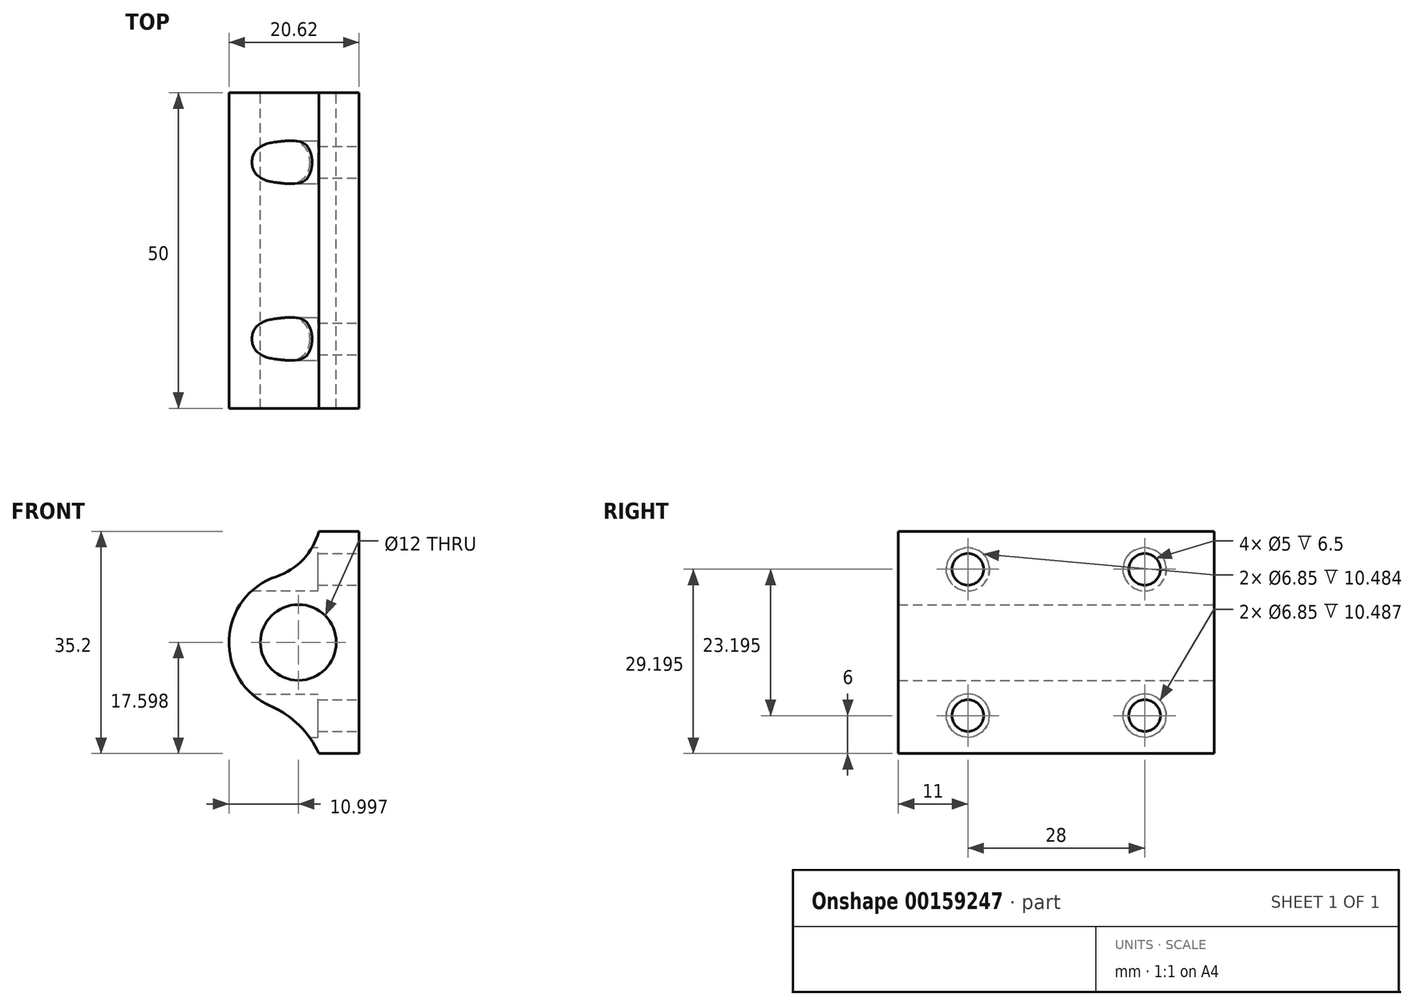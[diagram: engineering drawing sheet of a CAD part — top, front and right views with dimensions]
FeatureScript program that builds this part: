
annotation { "Feature Type Name" : "Feature", "Feature Type Description" : "" }
export const myFeature = defineFeature(function(context is Context, id is Id, definition is map)
    precondition{}
    {
        {
            var Q0;
            Q0=qCreatedBy(makeId("Front.planeOp"),FACE);
            var sketch = newSketch(context, id + "F0", { "sketchPlane" : qUnion([Q0])});
            skLineSegment(sketch, "E0", {"start": v(0, 35.2) * mm, "end": v(0, 0) * mm});
            skLineSegment(sketch, "E1", {"start": v(0, 0) * mm, "end": v(-6.38, 0) * mm});
            skLineSegment(sketch, "E2", {"start": v(0, 17.6) * mm, "end": v(-19.25, 17.6) * mm, "construction": true});
            skCircle(sketch, "E3", {"center": v(-9.62, 17.6) * mm, "radius": 6 * mm});
            skLineSegment(sketch, "E4", {"start": v(0, 35.2) * mm, "end": v(-6.38, 35.2) * mm});
            skPoint(sketch, "E5.orphan", {"position": v(-12.38, 22.93) * mm});
            skPoint(sketch, "E6.orphan", {"position": v(-12.38, 12.27) * mm});
            skArc(sketch, "E7.0", {"start": v(-13.1, 28.03) * mm, "mid": v(-20.61, 18.06) * mm, "end": v(-13.98, 7.5) * mm});
            skArc(sketch, "E8", {"start": v(-13.1, 28.03) * mm, "mid": v(-8.84, 30.76) * mm, "end": v(-6.38, 35.2) * mm});
            skArc(sketch, "E9", {"start": v(-6.38, 0) * mm, "mid": v(-9.47, 4.46) * mm, "end": v(-13.98, 7.5) * mm});
            skSolve(sketch);
        }
        {
            var Q0;
            Q0 = qSketchRegion(id + "F0", true);
            extrude(context, id + "F1", {"entities" : qUnion([Q0]), "depth" : 50 * mm});
        }
        {
            var Q0;
            Q0=makeQuery(id+"F1.opExtrude","SWEPT_FACE",FACE,{"disambiguationData":[OSD([sQuery(id+"F0.wireOp",EDGE,"E0")])]});
            var sketch = newSketch(context, id + "F2", { "sketchPlane" : qUnion([Q0])});
            skLineSegment(sketch, "E10.0", {"start": v(-50, 35.2) * mm, "end": v(0, 35.2) * mm, "construction": true});
            skLineSegment(sketch, "E11", {"start": v(-50, 23.6) * mm, "end": v(0, 23.6) * mm, "construction": true});
            skLineSegment(sketch, "E12", {"start": v(-50, 11.6) * mm, "end": v(0, 11.6) * mm, "construction": true});
            skLineSegment(sketch, "E13", {"start": v(-39, 35.2) * mm, "end": v(-39, 0) * mm, "construction": true});
            skLineSegment(sketch, "E14", {"start": v(-11, 35.2) * mm, "end": v(-11, 0) * mm, "construction": true});
            skCircle(sketch, "E15", {"center": v(-39, 29.2) * mm, "radius": 2.5 * mm});
            skCircle(sketch, "E16", {"center": v(-11, 29.2) * mm, "radius": 2.5 * mm});
            skLineSegment(sketch, "E17", {"start": v(-50, 17.6) * mm, "end": v(0, 17.6) * mm, "construction": true});
            skCircle(sketch, "E18.MirrorC", {"center": v(-39, 6) * mm, "radius": 2.5 * mm});
            skCircle(sketch, "E19.MirrorC", {"center": v(-11, 6) * mm, "radius": 2.5 * mm});
            skPoint(sketch, "E20.0.start.orphan", {"position": v(-50, 0) * mm});
            skPoint(sketch, "E21.0.end.orphan", {"position": v(0, 0) * mm});
            skSolve(sketch);
        }
        {
            var Q0;
            Q0 = qSketchRegion(id + "F2", true);
            extrude(context, id + "F3", {"entities" : qUnion([Q0]), "operationType" : NewBodyOperationType.REMOVE, "oppositeDirection" : true, "depth" : 25 * mm});
        }
        {
            var Q0;
            Q0=qCreatedBy(makeId("Right.planeOp"),FACE);
            cPlane(context, id + "F4", {"entities" : qUnion([Q0]), "cplaneType" : CPlaneType.OFFSET, "offset" : 6.5 * mm, "oppositeDirection" : true, "width" : 150 * mm, "height" : 150 * mm});
        }
        {
            var Q0;
            Q0=qCreatedBy(id+"F4.planeOp",FACE);
            var sketch = newSketch(context, id + "F5", { "sketchPlane" : qUnion([Q0])});
            skArc(sketch, "E22.0", {"start": v(-13, 7.5) * mm, "mid": v(-11, 3.5) * mm, "end": v(-9, 7.5) * mm});
            skArc(sketch, "E23.0", {"start": v(-8.79, 28.03) * mm, "mid": v(-11, 31.7) * mm, "end": v(-13.21, 28.03) * mm});
            skArc(sketch, "E24.0", {"start": v(-41, 7.5) * mm, "mid": v(-39, 3.5) * mm, "end": v(-37, 7.5) * mm});
            skArc(sketch, "E25.0", {"start": v(-36.79, 28.03) * mm, "mid": v(-39, 31.7) * mm, "end": v(-41.21, 28.03) * mm});
            skCircle(sketch, "E26", {"center": v(-11, 6) * mm, "radius": 3.42 * mm});
            skCircle(sketch, "E27", {"center": v(-39, 6) * mm, "radius": 3.42 * mm});
            skCircle(sketch, "E28", {"center": v(-11, 29.2) * mm, "radius": 3.42 * mm});
            skCircle(sketch, "E29", {"center": v(-39, 29.2) * mm, "radius": 3.42 * mm});
            skSolve(sketch);
        }
        {
            var Q0;
            Q0 = qSketchRegion(id + "F5", true);
            extrude(context, id + "F6", {"entities" : qUnion([Q0]), "operationType" : NewBodyOperationType.REMOVE, "oppositeDirection" : true, "depth" : 25 * mm});
        }
    });
